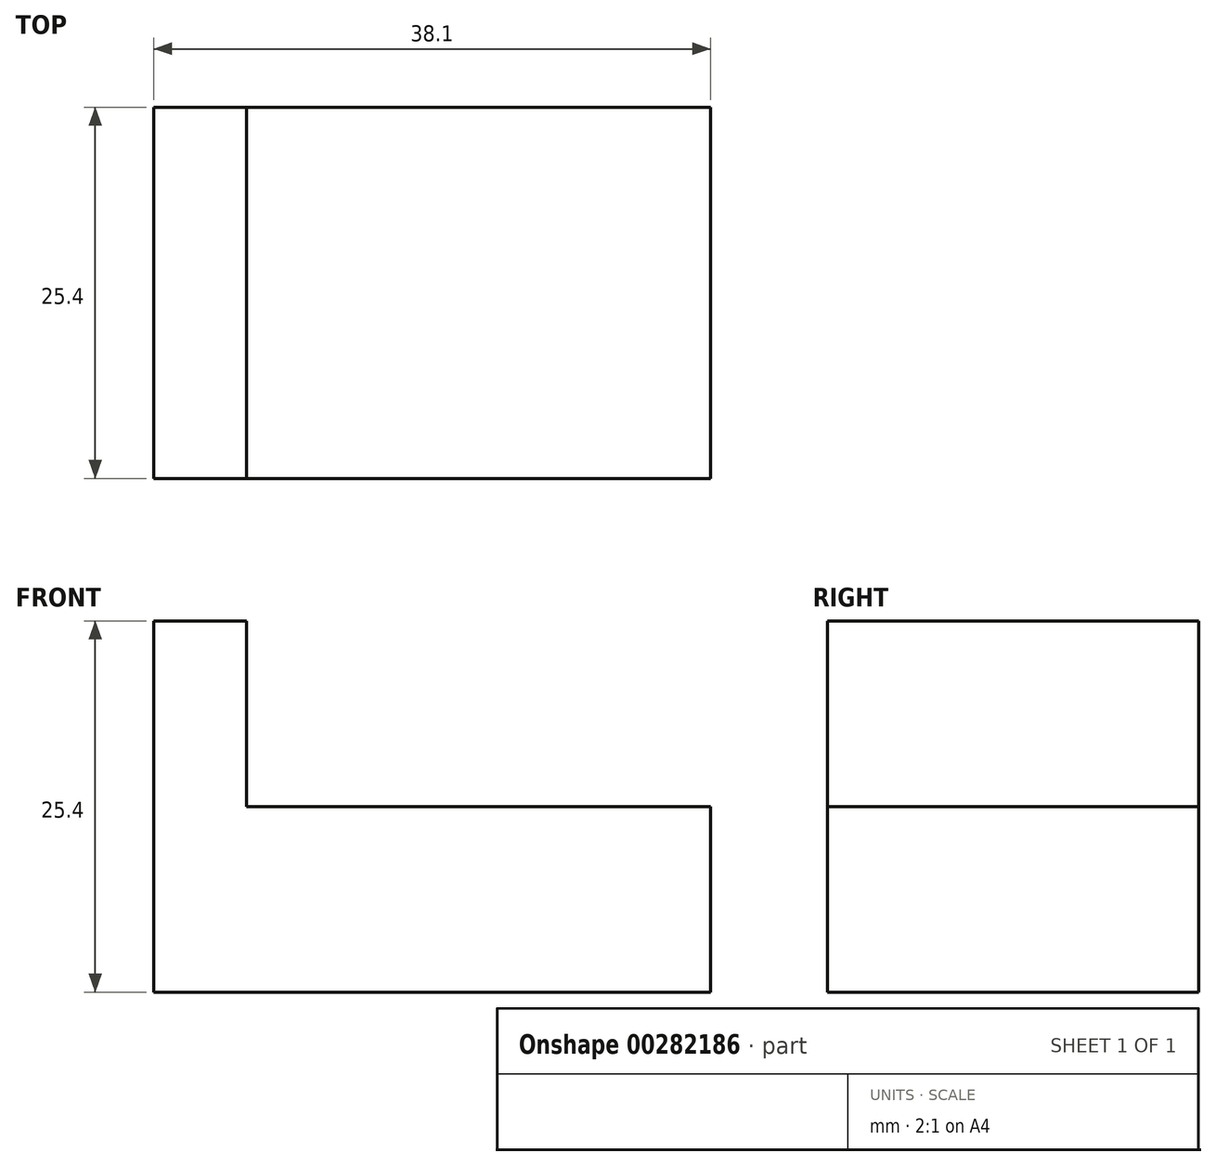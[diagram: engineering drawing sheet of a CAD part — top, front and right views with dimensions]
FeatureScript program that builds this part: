
annotation { "Feature Type Name" : "Feature", "Feature Type Description" : "" }
export const myFeature = defineFeature(function(context is Context, id is Id, definition is map)
    precondition{}
    {
        {
            var Q0;
            Q0=qCreatedBy(makeId("Front.planeOp"),FACE);
            var sketch = newSketch(context, id + "F0", { "sketchPlane" : qUnion([Q0])});
            skLineSegment(sketch, "E0", {"start": v(0, 0) * mm, "end": v(0, 25.4) * mm});
            skLineSegment(sketch, "E1", {"start": v(0, 25.4) * mm, "end": v(6.35, 25.4) * mm});
            skLineSegment(sketch, "E2", {"start": v(6.35, 25.4) * mm, "end": v(6.35, 12.7) * mm});
            skLineSegment(sketch, "E3", {"start": v(6.35, 12.7) * mm, "end": v(38.1, 12.7) * mm});
            skLineSegment(sketch, "E4", {"start": v(38.1, 12.7) * mm, "end": v(38.1, 0) * mm});
            skLineSegment(sketch, "E5", {"start": v(38.1, 0) * mm, "end": v(0, 0) * mm});
            skSolve(sketch);
        }
        {
            var Q0;
            Q0=makeQuery(id+"F0.imprint","IMPRINT",FACE,{"disambiguationData":[TD([[makeQuery(id+"F0.imprint","IMPRINT",EDGE,{"derivedFrom":sQuery(id+"F0.wireOp",EDGE,"E0")}),-1.0]])]});
            extrude(context, id + "F1", {"entities" : qUnion([Q0]), "depth" : 25.4 * mm});
        }
    });
